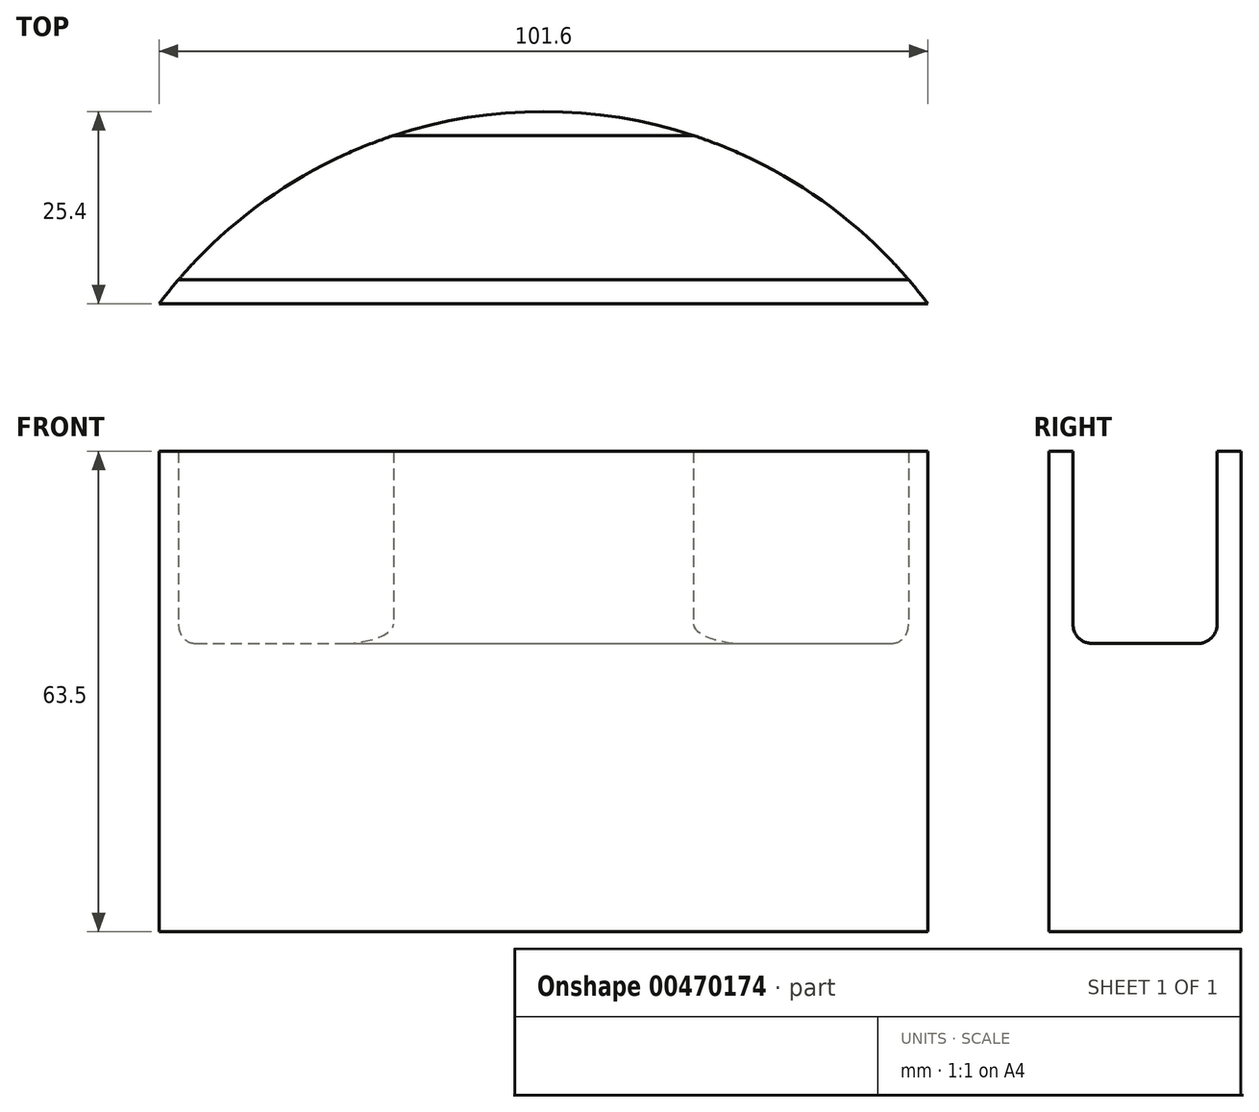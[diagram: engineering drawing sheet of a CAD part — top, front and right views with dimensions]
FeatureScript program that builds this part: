
annotation { "Feature Type Name" : "Feature", "Feature Type Description" : "" }
export const myFeature = defineFeature(function(context is Context, id is Id, definition is map)
    precondition{}
    {
        {
            var Q0;
            Q0=qCreatedBy(makeId("Top.planeOp"),FACE);
            var sketch = newSketch(context, id + "F0", { "sketchPlane" : qUnion([Q0])});
            skArc(sketch, "E0", {"start": v(50.8, 0) * mm, "mid": v(0, 25.4) * mm, "end": v(-50.8, 0) * mm});
            skLineSegment(sketch, "E1", {"start": v(-50.8, 0) * mm, "end": v(50.8, 0) * mm});
            skSolve(sketch);
        }
        {
            var Q0;
            Q0 = qSketchRegion(id + "F0", true);
            extrude(context, id + "F1", {"entities" : qUnion([Q0]), "depth" : 63.5 * mm});
        }
        {
            var Q0;
            Q0=qCreatedBy(makeId("Right.planeOp"),FACE);
            var sketch = newSketch(context, id + "F2", { "sketchPlane" : qUnion([Q0])});
            skLineSegment(sketch, "E2.bottom", {"start": v(3.17, 63.5) * mm, "end": v(22.23, 63.5) * mm});
            skLineSegment(sketch, "E2.top", {"start": v(3.18, 38.1) * mm, "end": v(22.23, 38.1) * mm});
            skLineSegment(sketch, "E2.left", {"start": v(3.17, 63.5) * mm, "end": v(3.18, 38.1) * mm});
            skLineSegment(sketch, "E2.right", {"start": v(22.23, 63.5) * mm, "end": v(22.23, 38.1) * mm});
            skSolve(sketch);
        }
        {
            var Q0;
            Q0 = qSketchRegion(id + "F2", true);
            extrude(context, id + "F3", {"entities" : qUnion([Q0]), "operationType" : NewBodyOperationType.REMOVE, "endBound" : BoundingType.SYMMETRIC, "oppositeDirection" : true, "depth" : 101.6 * mm});
        }
        {
            var Q0;
            Q0=makeQuery(id+"F3.boolean.opBoolean","COPY",EDGE,{"derivedFrom":makeQuery(id+"F3.opExtrude","SWEPT_EDGE",EDGE,{"disambiguationData":[OSD([sQuery(id+"F2.wireOp",EDGE,"E2.top"),sQuery(id+"F2.wireOp",EDGE,"E2.left")])]})});
            var Q1;
            Q1=makeQuery(id+"F3.boolean.opBoolean","COPY",EDGE,{"derivedFrom":makeQuery(id+"F3.opExtrude","SWEPT_EDGE",EDGE,{"disambiguationData":[OSD([sQuery(id+"F2.wireOp",EDGE,"E2.top"),sQuery(id+"F2.wireOp",EDGE,"E2.right")])]})});
            fillet(context, id + "F4", {"entities" : qUnion([Q0, Q1]), "radius" : 2.54 * mm, "tangentPropagation" : true, "allowEdgeOverflow" : false});
        }
    });
